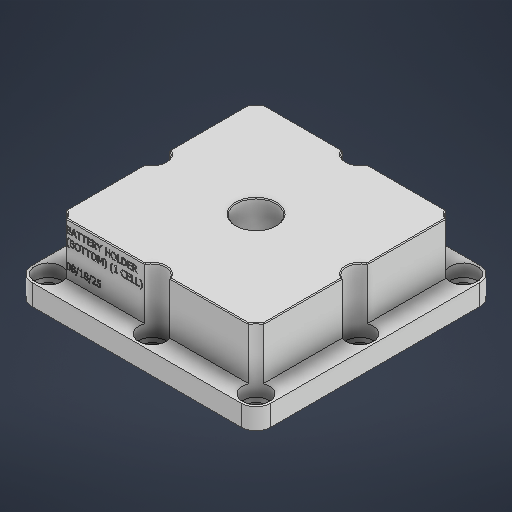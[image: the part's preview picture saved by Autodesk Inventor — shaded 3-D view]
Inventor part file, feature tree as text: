
AUTODESK INVENTOR PART (.ipt)
format: ipt  version: 2025 (Build 290162000, 162)  size: 896,512 bytes
history: native  units: in
note: dims shown in document units (in); Inventor stores cm internally (conversion verified against a paired STEP export)
features: sketch x5, extrude x3, hole x1, fillet x1, chamfer x1
ambient origin geometry x8: Origin, YZ Plane, XZ Plane, XY Plane, X Axis, Y Axis, Z Axis, Center Point
bodies: Solid1 (feature_tree)
feature tree (11):
  extrude  "Extrusion1"  Depth=4.5276in
  extrude  "Extrusion2"  Depth=3.7402in
  hole  "Hole3"  [1 undecoded]
  fillet  "Fillet1"  Radius=3.937in
  chamfer  "Chamfer1"  Distance=1.1811in
  extrude  "Extrusion3"  Depth=0.2805in
  sketch  "Sketch1"  dims[d0=4.5276in d1=4.5276in]
  sketch  "Sketch4"  dims[d2=0.3937in d3=0.0in d48=3.7402in]
  sketch  "Sketch5"  dims[d49=3.7402in d57=0.9843in d58=0.0in d156=3.937in]
  sketch  "Sketch Rectangular Pattern13"  dims[d158=0.2756in d159=1.1811in d161=1.9685in d162=1.1811in d164=1.9685in d167=0.2805in d168=0.2362in d169=0.5118in d170=1.2205in d171=90.0deg d172=0.315in d173=0.8108in d174=0.2805in d175=0.0157in d176=0.0787in d177=45.0deg d178=0.0787in d179=0.0in d180=0.748in]
  sketch  "Sketch6"  dims[d157=3.937in]
note: 1 required parameter value undecoded (feature->parameter linkage not recoverable at this tier; creation-order binding heuristic only, values carry confidence <= 0.55)
